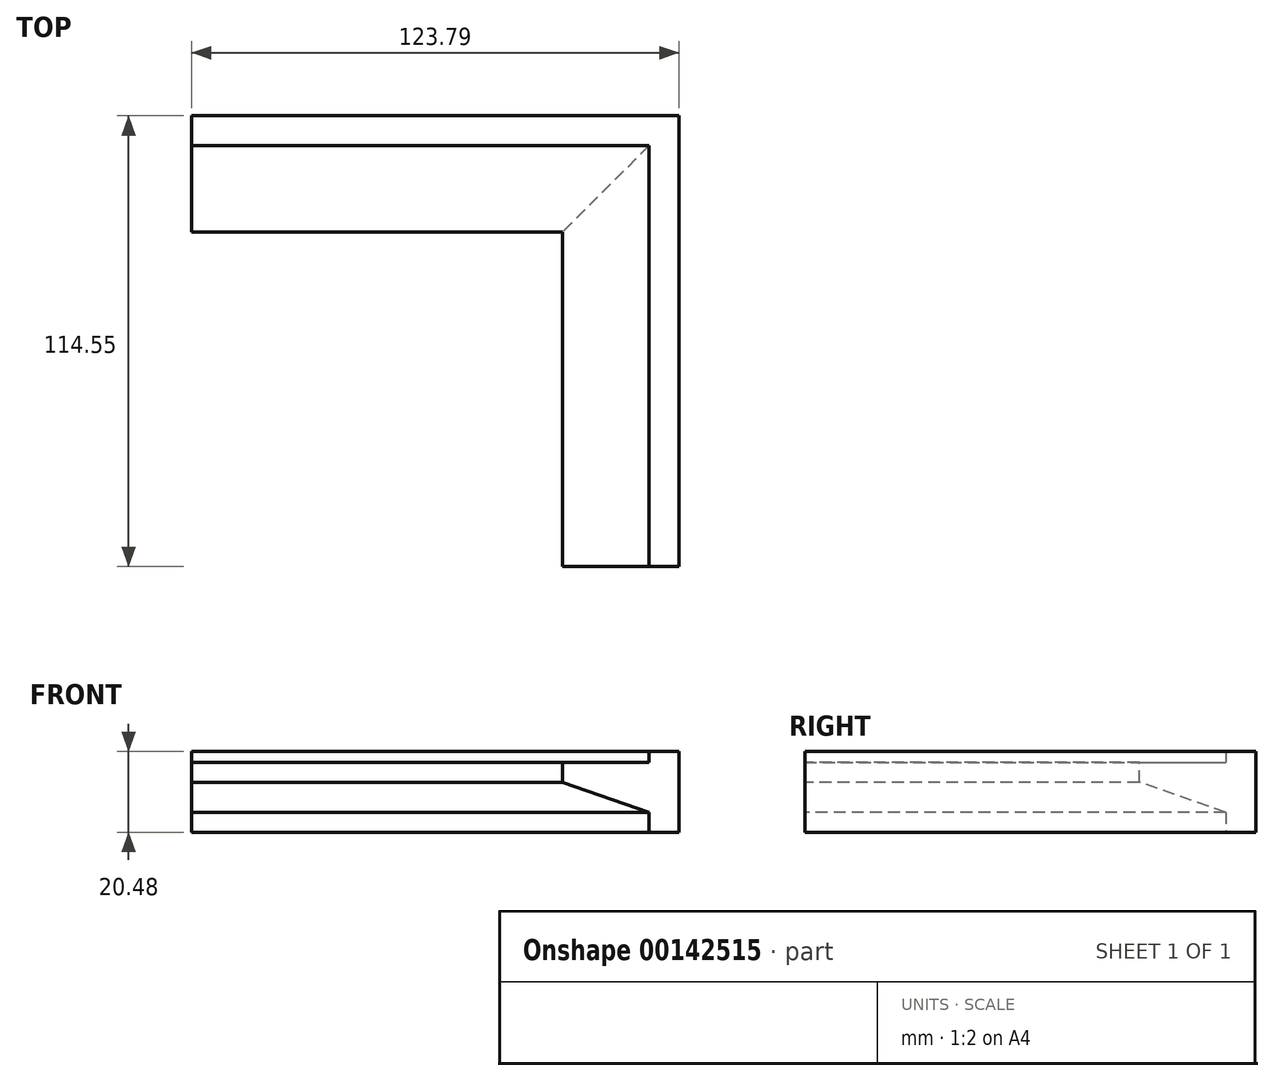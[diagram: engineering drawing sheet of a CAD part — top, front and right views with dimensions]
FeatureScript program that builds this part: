
annotation { "Feature Type Name" : "Feature", "Feature Type Description" : "" }
export const myFeature = defineFeature(function(context is Context, id is Id, definition is map)
    precondition{}
    {
        {
            var Q0;
            Q0=qCreatedBy(makeId("Front.planeOp"),FACE);
            var sketch = newSketch(context, id + "F0", { "sketchPlane" : qUnion([Q0])});
            skLineSegment(sketch, "E0.bottom", {"start": v(0, 0) * mm, "end": v(123.8, 0) * mm});
            skLineSegment(sketch, "E0.top", {"start": v(0, 20.48) * mm, "end": v(123.8, 20.48) * mm});
            skLineSegment(sketch, "E0.left", {"start": v(0, 0) * mm, "end": v(0, 20.48) * mm});
            skLineSegment(sketch, "E0.right", {"start": v(123.8, 0) * mm, "end": v(123.8, 20.48) * mm});
            skSolve(sketch);
        }
        {
            var Q0;
            Q0=makeQuery(id+"F0.imprint","IMPRINT",FACE,{"disambiguationData":[TD([[makeQuery(id+"F0.imprint","IMPRINT",EDGE,{"derivedFrom":sQuery(id+"F0.wireOp",EDGE,"E0.bottom")}),1.0]])]});
            extrude(context, id + "F1", {"entities" : qUnion([Q0]), "depth" : 7.62 * mm});
        }
        {
            var Q0;
            Q0=makeQuery(id+"F1.opExtrude","CAP_FACE",FACE,{"disambiguationData":[OSD([sQuery(id+"F0.wireOp",EDGE,"E0.bottom"),sQuery(id+"F0.wireOp",EDGE,"E0.top"),sQuery(id+"F0.wireOp",EDGE,"E0.left"),sQuery(id+"F0.wireOp",EDGE,"E0.right")])],"isStart":false});
            var sketch = newSketch(context, id + "F2", { "sketchPlane" : qUnion([Q0])});
            skLineSegment(sketch, "E1", {"start": v(116.17, 20.48) * mm, "end": v(116.17, 0) * mm});
            skSolve(sketch);
        }
        {
            var Q0;
            {var subQ0=sQuery(id+"F2.wireOp",EDGE,"E1");Q0=makeQuery(id+"F2.imprint","IMPRINT",FACE,{"disambiguationData":[TD([[makeQuery(id+"F2.imprint","IMPRINT",EDGE,{"derivedFrom":subQ0}),1.0]])]});}
            extrude(context, id + "F3", {"entities" : qUnion([Q0]), "operationType" : NewBodyOperationType.ADD, "depth" : 106.93 * mm});
        }
        {
            var Q0;
            Q0=makeQuery(id+"F1.opExtrude","SWEPT_FACE",FACE,{"disambiguationData":[OSD([sQuery(id+"F0.wireOp",EDGE,"E0.left")])]});
            var sketch = newSketch(context, id + "F4", { "sketchPlane" : qUnion([Q0])});
            skPoint(sketch, "E2", {"position": v(7.62, 5.08) * mm});
            skLineSegment(sketch, "E3", {"start": v(7.62, 0) * mm, "end": v(29.62, 12.7) * mm, "construction": true});
            skLineSegment(sketch, "E4", {"start": v(7.62, 5.08) * mm, "end": v(29.62, 12.7) * mm});
            skLineSegment(sketch, "E5", {"start": v(29.62, 12.7) * mm, "end": v(29.62, 17.78) * mm});
            skLineSegment(sketch, "E6", {"start": v(29.62, 17.78) * mm, "end": v(7.62, 17.78) * mm});
            skLineSegment(sketch, "E7", {"start": v(7.62, 5.08) * mm, "end": v(7.62, 17.78) * mm});
            skSolve(sketch);
        }
        {
            var Q0;
            Q0=makeQuery(id+"F4.imprint","IMPRINT",FACE,{"disambiguationData":[TD([[makeQuery(id+"F4.imprint","IMPRINT",EDGE,{"derivedFrom":sQuery(id+"F4.wireOp",EDGE,"E4")}),1.0]])]});
            var Q1;
            Q1=makeQuery(id+"F3.opExtrude","SWEPT_FACE",FACE,{"disambiguationData":[OSD([sQuery(id+"F2.wireOp",EDGE,"E1")])]});
            extrude(context, id + "F5", {"entities" : qUnion([Q0]), "operationType" : NewBodyOperationType.ADD, "endBound" : BoundingType.UP_TO_SURFACE, "oppositeDirection" : true, "endBoundEntityFace" : qUnion([Q1]), "depth" : 25.4 * mm});
        }
        {
            var Q0;
            Q0=makeQuery(id+"F3.opExtrude","CAP_FACE",FACE,{"disambiguationData":[OSD([sQuery(id+"F0.wireOp",EDGE,"E0.bottom"),sQuery(id+"F0.wireOp",EDGE,"E0.top"),sQuery(id+"F0.wireOp",EDGE,"E0.right"),sQuery(id+"F2.wireOp",EDGE,"E1")])],"isStart":false});
            var sketch = newSketch(context, id + "F6", { "sketchPlane" : qUnion([Q0])});
            skLineSegment(sketch, "E8", {"start": v(116.17, 0) * mm, "end": v(94.17, 12.7) * mm, "construction": true});
            skPoint(sketch, "E9", {"position": v(116.17, 5.08) * mm});
            skLineSegment(sketch, "E10", {"start": v(116.17, 5.08) * mm, "end": v(94.17, 12.7) * mm});
            skLineSegment(sketch, "E11", {"start": v(94.17, 12.7) * mm, "end": v(94.17, 17.78) * mm});
            skLineSegment(sketch, "E12", {"start": v(94.17, 17.78) * mm, "end": v(116.17, 17.78) * mm});
            skLineSegment(sketch, "E13", {"start": v(116.17, 17.78) * mm, "end": v(116.17, 5.08) * mm});
            skSolve(sketch);
        }
        {
            var Q0;
            Q0=makeQuery(id+"F6.imprint","IMPRINT",FACE,{"disambiguationData":[TD([[makeQuery(id+"F6.imprint","IMPRINT",EDGE,{"derivedFrom":sQuery(id+"F6.wireOp",EDGE,"E10")}),-1.0]])]});
            var Q1;
            {var subQ1=sQuery(id+"F0.wireOp",EDGE,"E0.top");var subQ2=sQuery(id+"F0.wireOp",EDGE,"E0.left");Q1=makeQuery(id+"F5.boolean.opBoolean","SPLIT",FACE,{"disambiguationData":[TD([makeQuery(id+"F1.opExtrude","SWEPT_FACE",FACE,{"disambiguationData":[OSD([subQ1])]})])],"derivedFrom":makeQuery(id+"F1.opExtrude","CAP_FACE",FACE,{"disambiguationData":[OSD([sQuery(id+"F0.wireOp",EDGE,"E0.bottom"),subQ1,subQ2,sQuery(id+"F0.wireOp",EDGE,"E0.right")])],"isStart":false})});}
            extrude(context, id + "F7", {"entities" : qUnion([Q0]), "operationType" : NewBodyOperationType.ADD, "endBound" : BoundingType.UP_TO_SURFACE, "oppositeDirection" : true, "endBoundEntityFace" : qUnion([Q1]), "depth" : 25.4 * mm});
        }
    });
